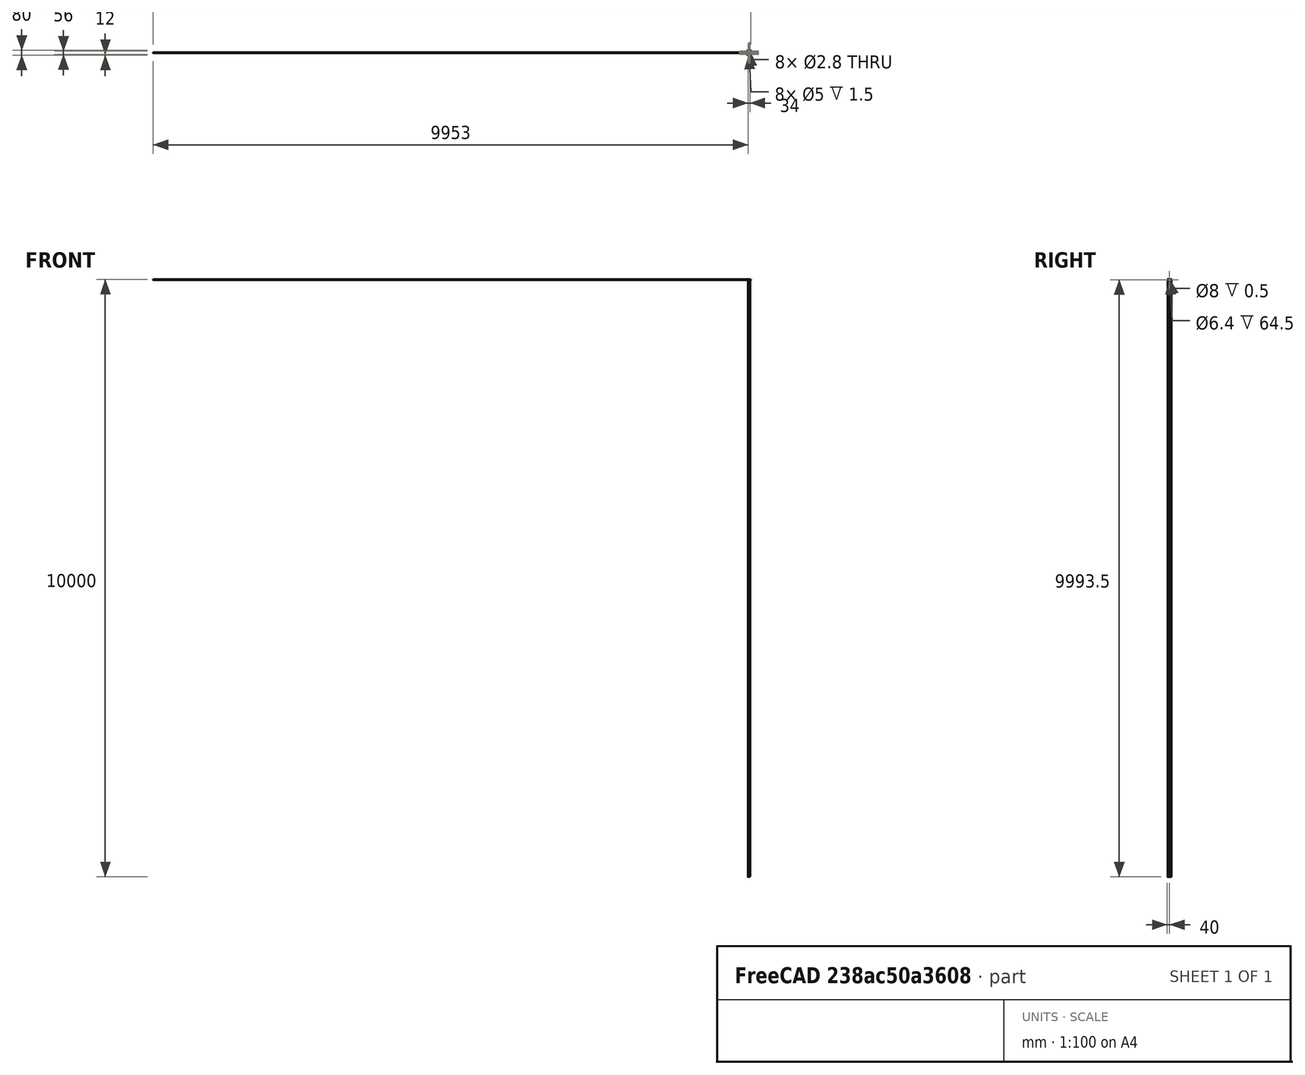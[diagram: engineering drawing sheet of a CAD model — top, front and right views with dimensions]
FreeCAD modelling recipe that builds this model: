
FCSTD DOCUMENT  (FreeCAD 0.16R)
Label: Mk1_2_top
License: All rights reserved
LicenseURL: http://en.wikipedia.org/wiki/All_rights_reserved
objects: Sketcher::SketchObject×7, PartDesign::Pocket×5, PartDesign::Pad×2, PartDesign::Fillet×1, PartDesign::Chamfer×1, Part::Cut×1, Mesh::Feature×1
note: 24 computed .brp shape members not serialized (recipe doc carries the construction recipe); baked Part::Feature solids carry a one-line shape summary decoded from their .brp

FEATURE [Sketcher::SketchObject] Sketch
  sketch-geometry (7):
    g0: LineSegment StartX=25 StartY=40 StartZ=0 EndX=25 EndY=-40 EndZ=0
    g1: LineSegment StartX=-40 StartY=10 StartZ=0 EndX=-20 EndY=40 EndZ=0
    g2: LineSegment StartX=-20 StartY=40 StartZ=0 EndX=25 EndY=40 EndZ=0
    g3: LineSegment StartX=25 StartY=40 StartZ=0 EndX=25 EndY=-40 EndZ=0
    g4: LineSegment StartX=25 StartY=-40 StartZ=0 EndX=-20 EndY=-40 EndZ=0
    g5: LineSegment StartX=-20 StartY=-40 StartZ=0 EndX=-40 EndY=-10 EndZ=0
    g6: LineSegment StartX=-40 StartY=-10 StartZ=0 EndX=-40 EndY=10 EndZ=0
  constraints (19):
    c: Coincident(g1,g2)
    c: Horizontal(g2)
    c: Coincident(g2,g3)
    c: Coincident(g3,g0)
    c: Vertical(g3)
    c: Coincident(g3,g4)
    c: Horizontal(g4)
    c: Coincident(g4,g5)
    c: Coincident(g5,g6)
    c: Coincident(g0,g2)
    c: Coincident(g1,g6)
    c: Distance(g-1,g0) = 25
    c: DistanceX(g1,g-1) = 20
    c: DistanceX(g1,g-1) = 40
    c: Vertical(g6)
    c: Symmetric(g1,g5,g-1)
    c: Symmetric(g4,g1,g-1)
    c: DistanceY(g1) = 10
    c: Distance(g0) = 80
FEATURE [PartDesign::Pad] Pad  label="Body"
  Length = 13
  Length2 = 100
  Sketch = -> Sketch
  Type = 0
FEATURE [Sketcher::SketchObject] Sketch001
  ExternalGeometry = -> [Pad]
  Placement = pos=(25,0,0) rot=(0.57735,0.57735,0.57735;2.0944rad)
  Support = -> Pad [Face1]
  sketch-geometry (1):
    g0: Circle CenterX=0 CenterY=6.5 CenterZ=0 NormalX=0 NormalY=0 NormalZ=1 Radius=3.2
  constraints (2):
    c: Symmetric(g-3,g-4,g0)
    c: Radius(g0) = 3.2
FEATURE [PartDesign::Pocket] Pocket  label="6.4through"
  Length = 20
  Sketch = -> Sketch001
  Type = 1
FEATURE [Sketcher::SketchObject] Sketch002
  ExternalGeometry = -> [Pocket]
  Placement = pos=(25,0,0) rot=(0.57735,0.57735,0.57735;2.0944rad)
  Support = -> Pocket [Face1]
  sketch-geometry (1):
    g0: Circle CenterX=0 CenterY=6.5 CenterZ=0 NormalX=0 NormalY=0 NormalZ=1 Radius=4
  constraints (2):
    c: Symmetric(g-4,g-3,g0)
    c: Radius(g0) = 4
FEATURE [PartDesign::Pocket] Pocket001  label="8mmBy15mm"
  Length = 0.5
  Sketch = -> Sketch002
  Type = 0
FEATURE [PartDesign::Fillet] Fillet
  Base = -> Pocket001 [Edge4,Edge17,Edge21,Edge20,Edge6,Edge1]
  Radius = 10
FEATURE [PartDesign::Chamfer] Chamfer
  Base = -> Fillet [Edge1,Edge6,Edge7,Edge8,Edge9,Edge10,Edge11,Edge12,Edge13,Edge14,Edge15,Edge16,Edge4,Edge18,Edge20,Edge21,Edge22,Edge23,Edge24,Edge25,Edge26,Edge27,Edge28,Edge29]
  Size = 1
FEATURE [Sketcher::SketchObject] Sketch003
  ExternalGeometry = -> [Chamfer]
  Placement = pos=(-40,0,0) rot=(0.57735,-0.57735,-0.57735;2.0944rad)
  Support = -> Chamfer [Face41]
  sketch-geometry (1):
    g0: Circle CenterX=0 CenterY=6.5 CenterZ=0 NormalX=0 NormalY=0 NormalZ=1 Radius=4.5
  constraints (2):
    c: Coincident(g0,g-3)
    c: Radius(g0) = 4.5
FEATURE [PartDesign::Pocket] Pocket002  label="9mmBy15mmEnd"
  Length = 15
  Sketch = -> Sketch003
  Type = 0
FEATURE [Sketcher::SketchObject] Sketch004
  Placement = pos=(0,0,13) rot=(0,0,1;0rad)
  Support = -> Pocket002 [Face12]
  sketch-geometry (8):
    g0: Circle CenterX=-10 CenterY=28 CenterZ=0 NormalX=0 NormalY=0 NormalZ=1 Radius=1.4
    g1: Circle CenterX=10 CenterY=28 CenterZ=0 NormalX=0 NormalY=0 NormalZ=1 Radius=1.4
    g2: Circle CenterX=-10 CenterY=-28 CenterZ=0 NormalX=0 NormalY=0 NormalZ=1 Radius=1.4
    g3: Circle CenterX=10 CenterY=-28 CenterZ=0 NormalX=0 NormalY=0 NormalZ=1 Radius=1.4
    g4: Circle CenterX=-22 CenterY=-10 CenterZ=0 NormalX=0 NormalY=0 NormalZ=1 Radius=1.4
    g5: Circle CenterX=12 CenterY=-10 CenterZ=0 NormalX=0 NormalY=0 NormalZ=1 Radius=1.4
    g6: Circle CenterX=12 CenterY=10 CenterZ=0 NormalX=0 NormalY=0 NormalZ=1 Radius=1.4
    g7: Circle CenterX=-22 CenterY=10 CenterZ=0 NormalX=0 NormalY=0 NormalZ=1 Radius=1.4
  constraints (13):
    c: Radius(g0) = 1.4
    c: Equal(g0, g1-g7) x7
    c: Symmetric(g6,g5,g-1)
    c: Symmetric(g4,g7,g-1)
    c: Symmetric(g1,g3,g-1)
    c: Symmetric(g1,g0,g-2)
    c: Symmetric(g3,g2,g-2)
    c: DistanceY(g7) = 10
    c: DistanceY(g6) = 10
    c: DistanceX(g6) = 12
    c: DistanceX(g7) = -22
    c: DistanceY(g1) = 28
    c: DistanceX(g1) = 10
FEATURE [PartDesign::Pocket] Pocket003  label="ScrewHolesThrough"
  Length = 5
  Sketch = -> Sketch004
  Type = 1
FEATURE [Sketcher::SketchObject] Sketch005
  ExternalGeometry = -> [Pocket003]
  Placement = pos=(0,0,13) rot=(0,0,1;0rad)
  Support = -> Pocket003 [Face12]
  sketch-geometry (8):
    g0: Circle CenterX=-10 CenterY=28 CenterZ=0 NormalX=0 NormalY=0 NormalZ=1 Radius=2.5
    g1: Circle CenterX=10 CenterY=28 CenterZ=0 NormalX=0 NormalY=0 NormalZ=1 Radius=2.5
    g2: Circle CenterX=12 CenterY=10 CenterZ=0 NormalX=0 NormalY=0 NormalZ=1 Radius=2.5
    g3: Circle CenterX=-22 CenterY=10 CenterZ=0 NormalX=0 NormalY=0 NormalZ=1 Radius=2.5
    g4: Circle CenterX=-22 CenterY=-10 CenterZ=0 NormalX=0 NormalY=0 NormalZ=1 Radius=2.5
    g5: Circle CenterX=-10 CenterY=-28 CenterZ=0 NormalX=0 NormalY=0 NormalZ=1 Radius=2.5
    g6: Circle CenterX=10 CenterY=-28 CenterZ=0 NormalX=0 NormalY=0 NormalZ=1 Radius=2.5
    g7: Circle CenterX=12 CenterY=-10 CenterZ=0 NormalX=0 NormalY=0 NormalZ=1 Radius=2.5
  constraints (16):
    c: Radius(g0) = 2.5
    c: Equal(g0,g1)
    c: Equal(g0,g3)
    c: Equal(g0,g4)
    c: Equal(g0,g2)
    c: Equal(g0,g5)
    c: Equal(g0,g6)
    c: Equal(g0,g7)
    c: Coincident(g0,g-4)
    c: Coincident(g1,g-3)
    c: Coincident(g3,g-5)
    c: Coincident(g2,g-6)
    c: Coincident(g4,g-8)
    c: Coincident(g5,g-9)
    c: Coincident(g6,g-10)
    c: Coincident(g7,g-7)
FEATURE [PartDesign::Pocket] Pocket004  label="CounterSinks"
  Length = 1.5
  Sketch = -> Sketch005
  Type = 0
FEATURE [Sketcher::SketchObject] Sketch006
  sketch-geometry (1):
    g0: Circle CenterX=0 CenterY=0 CenterZ=0 NormalX=0 NormalY=0 NormalZ=1 Radius=70
  constraints (2):
    c: Coincident(g0,g-1)
    c: Radius(g0) = 70
FEATURE [PartDesign::Pad] Pad001
  Length = 6.5
  Length2 = 100
  Sketch = -> Sketch006
  Type = 0
FEATURE [Part::Cut] Cut
  Base = -> Pocket004
  Tool = -> Pad001
FEATURE [Mesh::Feature] Mesh  label="Cut (Meshed)"
